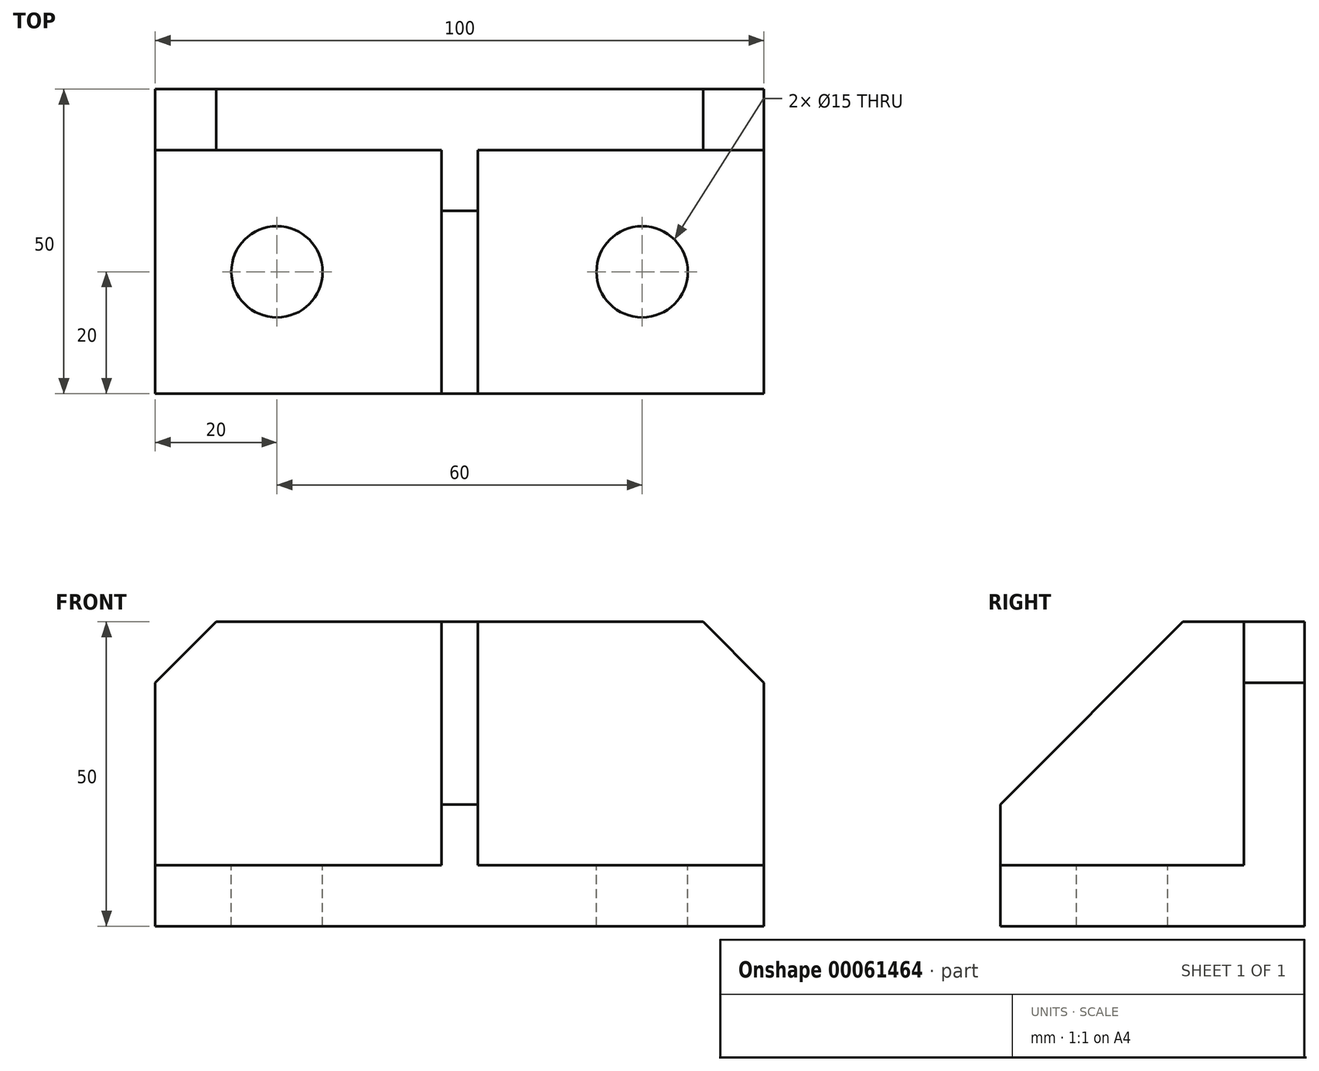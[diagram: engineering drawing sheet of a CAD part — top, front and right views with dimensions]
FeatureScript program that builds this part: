
annotation { "Feature Type Name" : "Feature", "Feature Type Description" : "" }
export const myFeature = defineFeature(function(context is Context, id is Id, definition is map)
    precondition{}
    {
        {
            var Q0;
            Q0=qCreatedBy(makeId("Top.planeOp"),FACE);
            var sketch = newSketch(context, id + "F0", { "sketchPlane" : qUnion([Q0])});
            skLineSegment(sketch, "E0.bottom", {"start": v(0, 0) * mm, "end": v(100, 0) * mm});
            skLineSegment(sketch, "E0.top", {"start": v(0, 50) * mm, "end": v(100, 50) * mm});
            skLineSegment(sketch, "E0.left", {"start": v(0, 0) * mm, "end": v(0, 50) * mm});
            skLineSegment(sketch, "E0.right", {"start": v(100, 0) * mm, "end": v(100, 50) * mm});
            skSolve(sketch);
        }
        {
            var Q0;
            Q0=makeQuery(id+"F0.imprint","IMPRINT",FACE,{"disambiguationData":[TD([[makeQuery(id+"F0.imprint","IMPRINT",EDGE,{"derivedFrom":sQuery(id+"F0.wireOp",EDGE,"E0.bottom")}),1.0]])]});
            extrude(context, id + "F1", {"entities" : qUnion([Q0]), "depth" : 50 * mm});
        }
        {
            var Q0;
            Q0=makeQuery(id+"F1.opExtrude","CAP_FACE",FACE,{"disambiguationData":[OSD([sQuery(id+"F0.wireOp",EDGE,"E0.bottom"),sQuery(id+"F0.wireOp",EDGE,"E0.top"),sQuery(id+"F0.wireOp",EDGE,"E0.left"),sQuery(id+"F0.wireOp",EDGE,"E0.right")])],"isStart":false});
            var sketch = newSketch(context, id + "F2", { "sketchPlane" : qUnion([Q0])});
            skLineSegment(sketch, "E1.bottom", {"start": v(0, 0) * mm, "end": v(47, 0) * mm});
            skLineSegment(sketch, "E1.top", {"start": v(0, 40) * mm, "end": v(47, 40) * mm});
            skLineSegment(sketch, "E1.left", {"start": v(0, 0) * mm, "end": v(0, 40) * mm});
            skLineSegment(sketch, "E1.right", {"start": v(47, 0) * mm, "end": v(47, 40) * mm});
            skSolve(sketch);
        }
        {
            var Q0;
            Q0=makeQuery(id+"F2.imprint","IMPRINT",FACE,{"disambiguationData":[TD([[makeQuery(id+"F2.imprint","IMPRINT",EDGE,{"derivedFrom":sQuery(id+"F2.wireOp",EDGE,"E1.bottom")}),1.0]])]});
            extrude(context, id + "F3", {"entities" : qUnion([Q0]), "operationType" : NewBodyOperationType.REMOVE, "oppositeDirection" : true, "depth" : 40 * mm});
        }
        {
            var Q0;
            Q0=makeQuery(id+"F1.opExtrude","CAP_FACE",FACE,{"disambiguationData":[OSD([sQuery(id+"F0.wireOp",EDGE,"E0.bottom"),sQuery(id+"F0.wireOp",EDGE,"E0.top"),sQuery(id+"F0.wireOp",EDGE,"E0.left"),sQuery(id+"F0.wireOp",EDGE,"E0.right")])],"isStart":false});
            var sketch = newSketch(context, id + "F4", { "sketchPlane" : qUnion([Q0])});
            skLineSegment(sketch, "E2.bottom", {"start": v(100, 0) * mm, "end": v(53, 0) * mm});
            skLineSegment(sketch, "E2.top", {"start": v(100, 40) * mm, "end": v(53, 40) * mm});
            skLineSegment(sketch, "E2.left", {"start": v(100, 0) * mm, "end": v(100, 40) * mm});
            skLineSegment(sketch, "E2.right", {"start": v(53, 0) * mm, "end": v(53, 40) * mm});
            skSolve(sketch);
        }
        {
            var Q0;
            Q0=makeQuery(id+"F4.imprint","IMPRINT",FACE,{"disambiguationData":[TD([[makeQuery(id+"F4.imprint","IMPRINT",EDGE,{"derivedFrom":sQuery(id+"F4.wireOp",EDGE,"E2.bottom")}),1.0]])]});
            extrude(context, id + "F5", {"entities" : qUnion([Q0]), "operationType" : NewBodyOperationType.REMOVE, "oppositeDirection" : true, "depth" : 40 * mm});
        }
        {
            var Q0;
            Q0=makeQuery(id+"F1.opExtrude","CAP_EDGE",EDGE,{"disambiguationData":[OSD([sQuery(id+"F0.wireOp",EDGE,"E0.bottom")])],"isStart":false});
            chamfer(context, id + "F6", {"entities" : qUnion([Q0]), "width" : 30 * mm, "tangentPropagation" : true});
        }
        {
            var Q0;
            Q0=makeQuery(id+"F3.boolean.opBoolean","COPY",FACE,{"derivedFrom":makeQuery(id+"F3.opExtrude","CAP_FACE",FACE,{"disambiguationData":[OSD([sQuery(id+"F2.wireOp",EDGE,"E1.bottom"),sQuery(id+"F2.wireOp",EDGE,"E1.top"),sQuery(id+"F2.wireOp",EDGE,"E1.left"),sQuery(id+"F2.wireOp",EDGE,"E1.right")])],"isStart":false})});
            var sketch = newSketch(context, id + "F7", { "sketchPlane" : qUnion([Q0])});
            skCircle(sketch, "E3", {"center": v(20, 20) * mm, "radius": 7.5 * mm});
            skSolve(sketch);
        }
        {
            var Q0;
            Q0=makeQuery(id+"F7.imprint","IMPRINT",FACE,{"disambiguationData":[TD([[makeQuery(id+"F7.imprint","IMPRINT",EDGE,{"derivedFrom":sQuery(id+"F7.wireOp",EDGE,"E3")}),1.0]])]});
            var Q1;
            Q1=sQuery(id+"F7.wireOp",EDGE,"E3");
            extrude(context, id + "F8", {"entities" : qUnion([Q0]), "operationType" : NewBodyOperationType.REMOVE, "surfaceEntities" : qUnion([Q1]), "oppositeDirection" : true, "depth" : 10 * mm});
        }
        {
            var Q0;
            Q0=makeQuery(id+"F5.boolean.opBoolean","COPY",FACE,{"derivedFrom":makeQuery(id+"F5.opExtrude","CAP_FACE",FACE,{"disambiguationData":[OSD([sQuery(id+"F4.wireOp",EDGE,"E2.bottom"),sQuery(id+"F4.wireOp",EDGE,"E2.top"),sQuery(id+"F4.wireOp",EDGE,"E2.left"),sQuery(id+"F4.wireOp",EDGE,"E2.right")])],"isStart":false})});
            var sketch = newSketch(context, id + "F9", { "sketchPlane" : qUnion([Q0])});
            skCircle(sketch, "E4", {"center": v(80, 20) * mm, "radius": 7.5 * mm});
            skSolve(sketch);
        }
        {
            var Q0;
            Q0=makeQuery(id+"F9.imprint","IMPRINT",FACE,{"disambiguationData":[TD([[makeQuery(id+"F9.imprint","IMPRINT",EDGE,{"derivedFrom":sQuery(id+"F9.wireOp",EDGE,"E4")}),1.0]])]});
            var Q1;
            Q1=sQuery(id+"F9.wireOp",EDGE,"E4");
            extrude(context, id + "F10", {"entities" : qUnion([Q0]), "operationType" : NewBodyOperationType.REMOVE, "surfaceEntities" : qUnion([Q1]), "oppositeDirection" : true, "depth" : 10 * mm});
        }
        {
            var Q0;
            Q0=makeQuery(id+"F1.opExtrude","CAP_EDGE",EDGE,{"disambiguationData":[OSD([sQuery(id+"F0.wireOp",EDGE,"E0.left")])],"isStart":false});
            var Q1;
            Q1=makeQuery(id+"F1.opExtrude","CAP_EDGE",EDGE,{"disambiguationData":[OSD([sQuery(id+"F0.wireOp",EDGE,"E0.right")])],"isStart":false});
            chamfer(context, id + "F11", {"entities" : qUnion([Q0, Q1]), "width" : 10 * mm, "tangentPropagation" : true});
        }
    });
